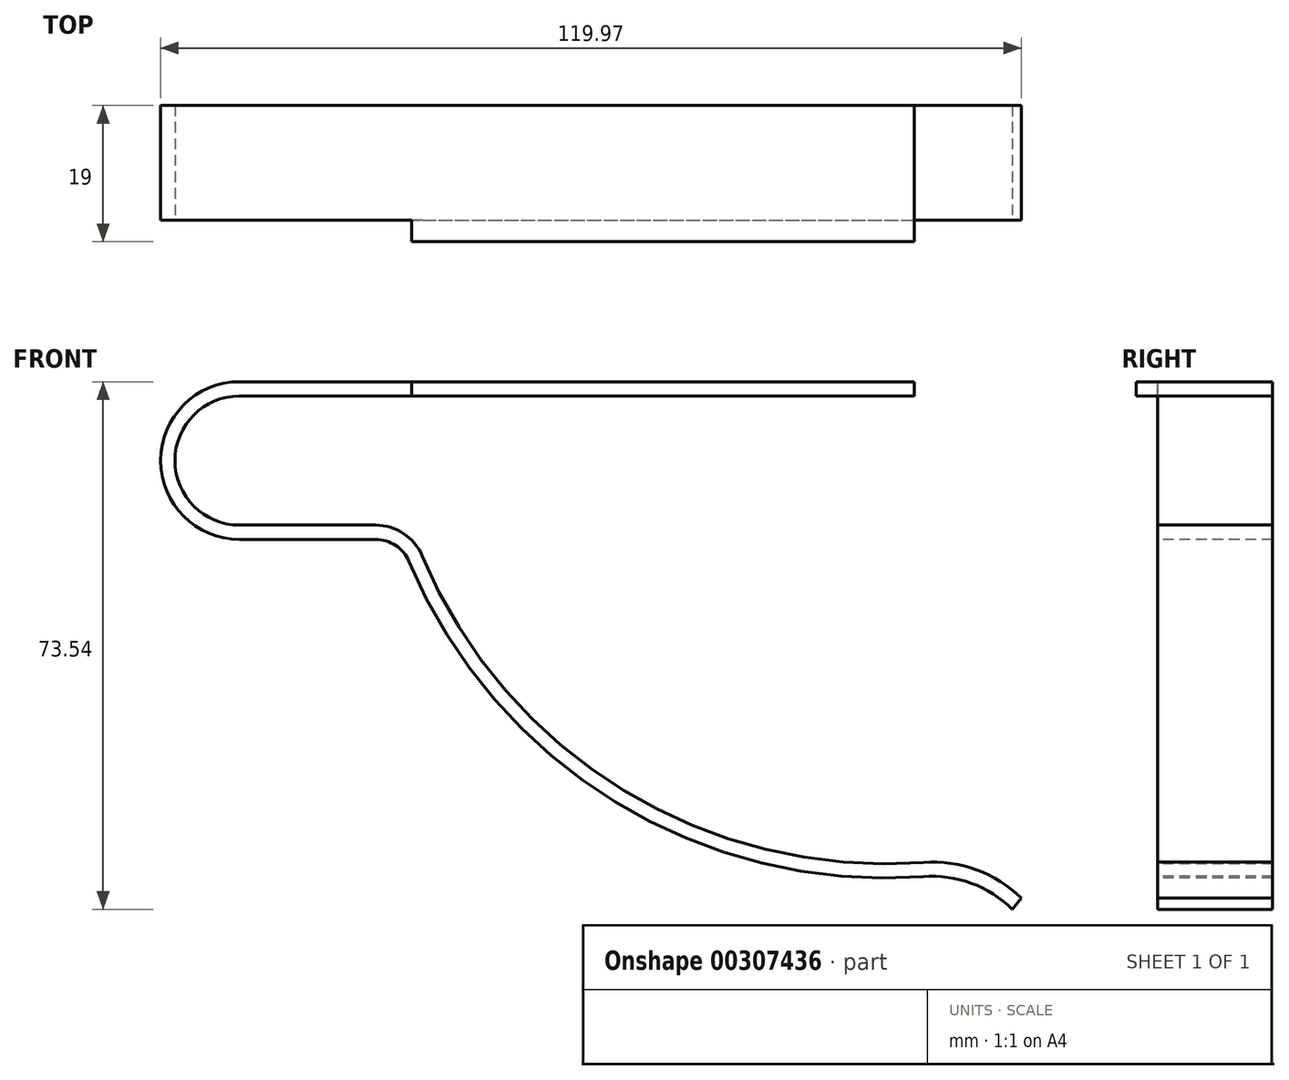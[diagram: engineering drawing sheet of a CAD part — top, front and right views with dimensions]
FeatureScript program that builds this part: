
annotation { "Feature Type Name" : "Feature", "Feature Type Description" : "" }
export const myFeature = defineFeature(function(context is Context, id is Id, definition is map)
    precondition{}
    {
        {
            var Q0;
            Q0=qCreatedBy(makeId("Front.planeOp"),FACE);
            var sketch = newSketch(context, id + "F0", { "sketchPlane" : qUnion([Q0])});
            skArc(sketch, "E0", {"start": v(0, 11) * mm, "mid": v(-11, 0) * mm, "end": v(0, -11) * mm});
            skLineSegment(sketch, "E1", {"start": v(0, 11) * mm, "end": v(94, 11) * mm});
            skLineSegment(sketch, "E2", {"start": v(0, -11) * mm, "end": v(19, -11) * mm});
            skArc(sketch, "E3", {"start": v(23.61, -14.06) * mm, "mid": v(52.37, -47.59) * mm, "end": v(95.3, -58) * mm});
            skPoint(sketch, "E4.visualSharp", {"position": v(22.4, -11) * mm});
            skArc(sketch, "E4.filletArc", {"start": v(23.61, -14.06) * mm, "mid": v(21.77, -11.84) * mm, "end": v(19, -11) * mm});
            skLineSegment(sketch, "E5.0", {"start": v(0, 9) * mm, "end": v(94, 9) * mm});
            skArc(sketch, "E5.1", {"start": v(0, 9) * mm, "mid": v(-9, 0) * mm, "end": v(0, -9) * mm});
            skArc(sketch, "E5.3", {"start": v(25.45, -13.3) * mm, "mid": v(53.48, -45.92) * mm, "end": v(95.3, -56) * mm});
            skArc(sketch, "E5.4", {"start": v(25.45, -13.3) * mm, "mid": v(22.88, -10.17) * mm, "end": v(19, -9) * mm});
            skLineSegment(sketch, "E5.5", {"start": v(0, -9) * mm, "end": v(19, -9) * mm});
            skLineSegment(sketch, "E6", {"start": v(94, 11) * mm, "end": v(94, 9) * mm});
            skLineSegment(sketch, "E7", {"start": v(111.83, -61) * mm, "end": v(123.84, -61) * mm});
            skPoint(sketch, "E8.end.orphan", {"position": v(111.83, -61) * mm});
            skPoint(sketch, "E9.orphan", {"position": v(111.25, -61) * mm});
            skArc(sketch, "E10", {"start": v(108.97, -61) * mm, "mid": v(102.67, -57.04) * mm, "end": v(95.3, -56) * mm});
            skArc(sketch, "E11.0", {"start": v(107.68, -62.54) * mm, "mid": v(101.98, -58.92) * mm, "end": v(95.3, -58) * mm});
            skLineSegment(sketch, "E12", {"start": v(108.97, -61) * mm, "end": v(107.68, -62.54) * mm});
            skSolve(sketch);
        }
        {
            var Q0;
            Q0 = qSketchRegion(id + "F0", true);
            extrude(context, id + "F1", {"entities" : qUnion([Q0]), "oppositeDirection" : true, "depth" : 16 * mm});
        }
        {
            var Q0;
            Q0=makeQuery(id+"F1.opExtrude","SWEPT_FACE",FACE,{"disambiguationData":[OSD([sQuery(id+"F0.wireOp",EDGE,"E1")])]});
            var sketch = newSketch(context, id + "F2", { "sketchPlane" : qUnion([Q0])});
            skLineSegment(sketch, "E13.bottom", {"start": v(94, 0) * mm, "end": v(24, 0) * mm});
            skLineSegment(sketch, "E13.top", {"start": v(94, -3) * mm, "end": v(24, -3) * mm});
            skLineSegment(sketch, "E13.left", {"start": v(94, 0) * mm, "end": v(94, -3) * mm});
            skLineSegment(sketch, "E13.right", {"start": v(24, 0) * mm, "end": v(24, -3) * mm});
            skSolve(sketch);
        }
        {
            var Q0;
            Q0 = qSketchRegion(id + "F2", true);
            extrude(context, id + "F3", {"entities" : qUnion([Q0]), "operationType" : NewBodyOperationType.ADD, "oppositeDirection" : true, "depth" : 2 * mm});
        }
    });
